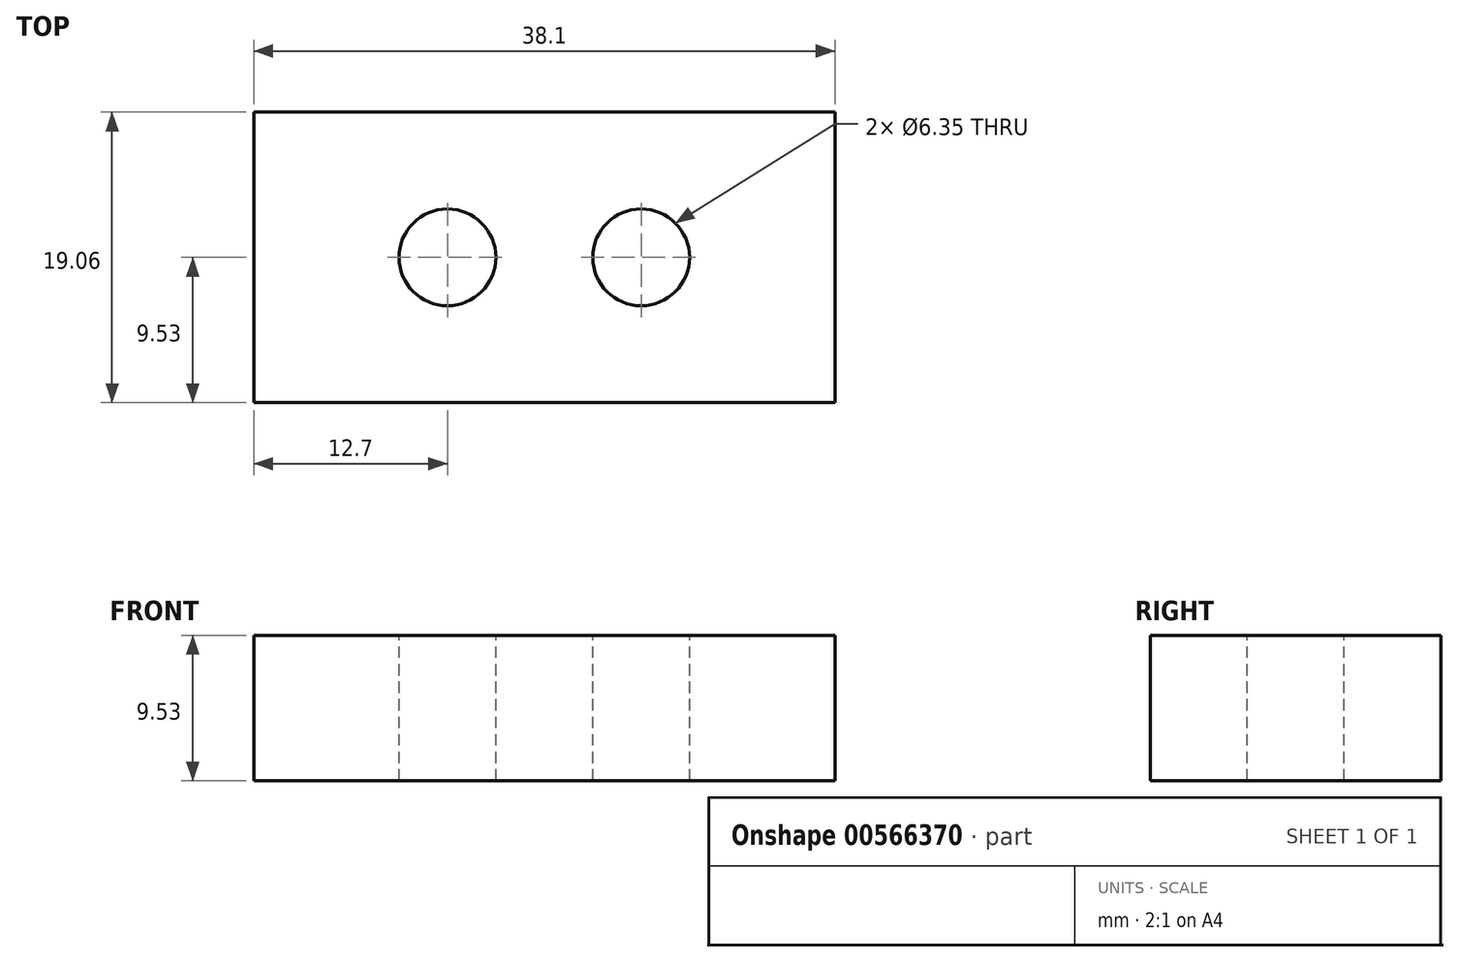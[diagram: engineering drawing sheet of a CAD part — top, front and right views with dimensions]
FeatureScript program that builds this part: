
annotation { "Feature Type Name" : "Feature", "Feature Type Description" : "" }
export const myFeature = defineFeature(function(context is Context, id is Id, definition is map)
    precondition{}
    {
        {
            var Q0;
            Q0=qCreatedBy(makeId("Top.planeOp"),FACE);
            var sketch = newSketch(context, id + "F0", { "sketchPlane" : qUnion([Q0])});
            skLineSegment(sketch, "E0.bottom", {"start": v(-19.05, 9.53) * mm, "end": v(19.05, 9.53) * mm});
            skLineSegment(sketch, "E0.top", {"start": v(-19.05, -9.53) * mm, "end": v(19.05, -9.52) * mm});
            skLineSegment(sketch, "E0.left", {"start": v(-19.05, 9.53) * mm, "end": v(-19.05, -9.53) * mm});
            skLineSegment(sketch, "E0.right", {"start": v(19.05, 9.53) * mm, "end": v(19.05, -9.52) * mm});
            skSolve(sketch);
        }
        {
            var Q0;
            Q0=makeQuery(id+"F0.imprint","IMPRINT",FACE,{"disambiguationData":[TD([[makeQuery(id+"F0.imprint","IMPRINT",EDGE,{"derivedFrom":sQuery(id+"F0.wireOp",EDGE,"E0.bottom")}),-1.0]])]});
            extrude(context, id + "F1", {"entities" : qUnion([Q0]), "depth" : 9.52 * mm, "offsetDistance" : 25.4 * mm});
        }
        {
            var Q0;
            Q0=makeQuery(id+"F1.opExtrude","CAP_FACE",FACE,{"disambiguationData":[OSD([sQuery(id+"F0.wireOp",EDGE,"E0.bottom"),sQuery(id+"F0.wireOp",EDGE,"E0.top"),sQuery(id+"F0.wireOp",EDGE,"E0.left"),sQuery(id+"F0.wireOp",EDGE,"E0.right")])],"isStart":false});
            var sketch = newSketch(context, id + "F2", { "sketchPlane" : qUnion([Q0])});
            skCircle(sketch, "E1", {"center": v(-6.35, 0) * mm, "radius": 3.18 * mm});
            skCircle(sketch, "E2", {"center": v(6.35, 0) * mm, "radius": 3.18 * mm});
            skSolve(sketch);
        }
        {
            var Q0;
            Q0=makeQuery(id+"F2.imprint","IMPRINT",FACE,{"disambiguationData":[TD([[makeQuery(id+"F2.imprint","IMPRINT",EDGE,{"derivedFrom":sQuery(id+"F2.wireOp",EDGE,"E1")}),1.0]])]});
            var Q1;
            Q1=makeQuery(id+"F2.imprint","IMPRINT",FACE,{"disambiguationData":[TD([[makeQuery(id+"F2.imprint","IMPRINT",EDGE,{"derivedFrom":sQuery(id+"F2.wireOp",EDGE,"E2")}),1.0]])]});
            extrude(context, id + "F3", {"entities" : qUnion([Q0, Q1]), "operationType" : NewBodyOperationType.REMOVE, "oppositeDirection" : true, "depth" : 25.4 * mm, "offsetDistance" : 25.4 * mm});
        }
    });
